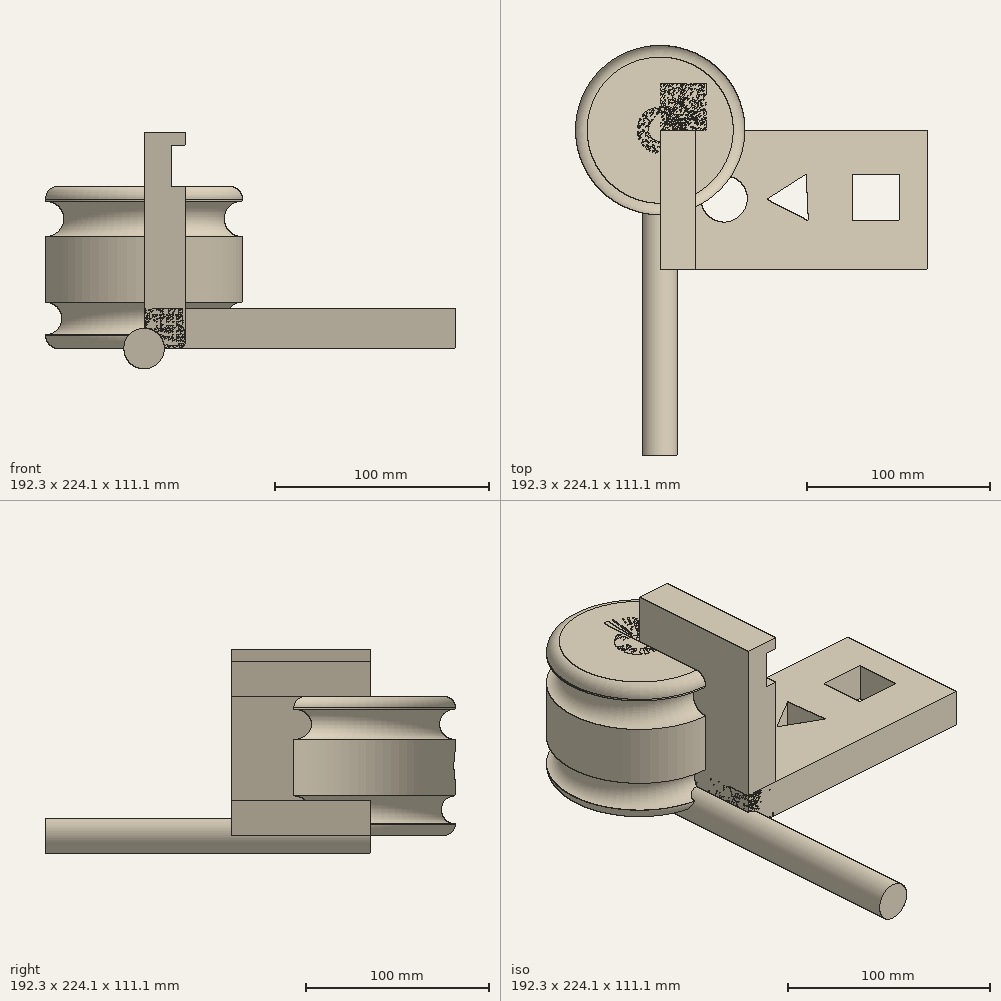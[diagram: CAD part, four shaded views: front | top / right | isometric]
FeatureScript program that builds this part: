
annotation { "Feature Type Name" : "Feature", "Feature Type Description" : "" }
export const myFeature = defineFeature(function(context is Context, id is Id, definition is map)
    precondition{}
    {
        {
            var Q0;
            Q0=qCreatedBy(makeId("Top.planeOp"),FACE);
            var sketch = newSketch(context, id + "F0", { "sketchPlane" : qUnion([Q0])});
            skCircle(sketch, "E0", {"center": v(0, 0) * mm, "radius": 12.7 * mm});
            skSolve(sketch);
        }
        {
            var Q0;
            Q0 = qSketchRegion(id + "F0", true);
            extrude(context, id + "F1", {"entities" : qUnion([Q0]), "depth" : 76.2 * mm, "offsetDistance" : 25.4 * mm});
        }
        {
            var Q0;
            Q0=qCreatedBy(makeId("Top.planeOp"),FACE);
            var sketch = newSketch(context, id + "F2", { "sketchPlane" : qUnion([Q0])});
            skLineSegment(sketch, "E1.bottom", {"start": v(0, 0) * mm, "end": v(25.4, 0) * mm});
            skLineSegment(sketch, "E1.top", {"start": v(0, 25.4) * mm, "end": v(25.4, 25.4) * mm});
            skLineSegment(sketch, "E1.left", {"start": v(0, 0) * mm, "end": v(0, 25.4) * mm});
            skLineSegment(sketch, "E1.right", {"start": v(25.4, 0) * mm, "end": v(25.4, 25.4) * mm});
            skSolve(sketch);
        }
        {
            var Q0;
            Q0 = qSketchRegion(id + "F2", true);
            extrude(context, id + "F3", {"entities" : qUnion([Q0]), "depth" : 76.2 * mm, "offsetDistance" : 25.4 * mm});
        }
        {
            var Q0;
            Q0=qCreatedBy(makeId("Top.planeOp"),FACE);
            var sketch = newSketch(context, id + "F4", { "sketchPlane" : qUnion([Q0])});
            skLineSegment(sketch, "E2", {"start": v(0, 0) * mm, "end": v(12.7, 22) * mm});
            skLineSegment(sketch, "E3", {"start": v(12.7, 22) * mm, "end": v(25.4, 0) * mm});
            skLineSegment(sketch, "E4", {"start": v(25.4, 0) * mm, "end": v(0, 0) * mm});
            skSolve(sketch);
        }
        {
            var Q0;
            Q0=makeQuery(id+"F4.imprint","IMPRINT",FACE,{"disambiguationData":[TD([[makeQuery(id+"F4.imprint","IMPRINT",EDGE,{"derivedFrom":sQuery(id+"F4.wireOp",EDGE,"E2")}),-1.0]])]});
            extrude(context, id + "F5", {"entities" : qUnion([Q0]), "depth" : 76.2 * mm, "offsetDistance" : 25.4 * mm});
        }
        {
            var Q0;
            Q0=qCreatedBy(makeId("Top.planeOp"),FACE);
            var sketch = newSketch(context, id + "F6", { "sketchPlane" : qUnion([Q0])});
            skLineSegment(sketch, "E5.bottom", {"start": v(0, 0) * mm, "end": v(146.05, 0) * mm});
            skLineSegment(sketch, "E5.top", {"start": v(0, -76.2) * mm, "end": v(146.05, -76.2) * mm});
            skLineSegment(sketch, "E5.left", {"start": v(0, 0) * mm, "end": v(0, -76.2) * mm});
            skLineSegment(sketch, "E5.right", {"start": v(146.05, 0) * mm, "end": v(146.05, -76.2) * mm});
            skCircle(sketch, "E6", {"center": v(34.93, -37.54) * mm, "radius": 12.7 * mm});
            skLineSegment(sketch, "E7.bottom", {"start": v(105.15, -49.45) * mm, "end": v(130.55, -49.45) * mm});
            skLineSegment(sketch, "E7.top", {"start": v(105.15, -24.05) * mm, "end": v(130.55, -24.05) * mm});
            skLineSegment(sketch, "E7.left", {"start": v(105.15, -49.45) * mm, "end": v(105.15, -24.05) * mm});
            skLineSegment(sketch, "E7.right", {"start": v(130.55, -49.45) * mm, "end": v(130.55, -24.05) * mm});
            skCircle(sketch, "E8.cCircle", {"center": v(73.03, -37.17) * mm, "radius": 7.33 * mm, "construction": true});
            skLineSegment(sketch, "E8.0", {"start": v(79.75, -24.13) * mm, "end": v(80.96, -49.5) * mm});
            skLineSegment(sketch, "E8.1", {"start": v(80.96, -49.5) * mm, "end": v(58.38, -37.86) * mm});
            skLineSegment(sketch, "E8.2", {"start": v(58.38, -37.86) * mm, "end": v(79.75, -24.13) * mm});
            skPoint(sketch, "E8.0.midPoint", {"position": v(80.35, -36.82) * mm});
            skSolve(sketch);
        }
        {
            var Q0;
            Q0 = qSketchRegion(id + "F6", true);
            extrude(context, id + "F7", {"entities" : qUnion([Q0]), "depth" : 19.05 * mm, "offsetDistance" : 25.4 * mm});
        }
        {
            var Q0;
            Q0=qCreatedBy(makeId("Front.planeOp"),FACE);
            var sketch = newSketch(context, id + "F8", { "sketchPlane" : qUnion([Q0])});
            skLineSegment(sketch, "E9.bottom", {"start": v(0, 0) * mm, "end": v(19.3, 0) * mm});
            skLineSegment(sketch, "E9.top", {"start": v(0, 101.6) * mm, "end": v(19.3, 101.6) * mm});
            skLineSegment(sketch, "E9.left", {"start": v(0, 0) * mm, "end": v(0, 101.6) * mm});
            skLineSegment(sketch, "E9.right", {"start": v(19.3, 0) * mm, "end": v(19.3, 101.6) * mm});
            skLineSegment(sketch, "E10.bottom", {"start": v(19.3, 95.25) * mm, "end": v(12.95, 95.25) * mm});
            skLineSegment(sketch, "E10.top", {"start": v(19.3, 76.2) * mm, "end": v(12.95, 76.2) * mm});
            skLineSegment(sketch, "E10.left", {"start": v(19.3, 95.25) * mm, "end": v(19.3, 76.2) * mm});
            skLineSegment(sketch, "E10.right", {"start": v(12.95, 95.25) * mm, "end": v(12.95, 76.2) * mm});
            skSolve(sketch);
        }
        {
            var Q0;
            {var subQ1=sQuery(id+"F8.wireOp",EDGE,"E9.bottom");Q0=makeQuery(id+"F8.imprint","IMPRINT",FACE,{"disambiguationData":[TD([[makeQuery(id+"F8.imprint","IMPRINT",EDGE,{"derivedFrom":subQ1}),1.0]])]});}
            var Q1;
            Q1 = qSketchRegion(id + "F10", true);
            extrude(context, id + "F9", {"entities" : qUnion([Q0, Q1]), "depth" : 76.2 * mm, "offsetDistance" : 25.4 * mm});
        }
        {
            var Q0;
            Q0=qCreatedBy(makeId("Front.planeOp"),FACE);
            var sketch = newSketch(context, id + "F10", { "sketchPlane" : qUnion([Q0])});
            skLineSegment(sketch, "E11.bottom", {"start": v(6.35, 0) * mm, "end": v(39.94, 0) * mm});
            skLineSegment(sketch, "E11.top", {"start": v(6.35, 76.2) * mm, "end": v(39.94, 76.2) * mm});
            skLineSegment(sketch, "E11.left", {"start": v(0, 6.35) * mm, "end": v(0, 69.85) * mm});
            skLineSegment(sketch, "E11.right", {"start": v(46.29, 6.35) * mm, "end": v(46.29, 69.85) * mm});
            skCircle(sketch, "E12", {"center": v(46.29, 86.97) * mm, "radius": 6.35 * mm});
            skCircle(sketch, "E13", {"center": v(45.89, 60.82) * mm, "radius": 8.2 * mm});
            skCircle(sketch, "E14", {"center": v(46.29, 14.1) * mm, "radius": 7.66 * mm});
            skPoint(sketch, "E15.visualSharp", {"position": v(46.29, 0) * mm});
            skArc(sketch, "E15.filletArc", {"start": v(39.94, 0) * mm, "mid": v(44.43, 1.86) * mm, "end": v(46.29, 6.35) * mm});
            skPoint(sketch, "E16.visualSharp", {"position": v(46.29, 76.2) * mm});
            skArc(sketch, "E16.filletArc", {"start": v(46.29, 69.85) * mm, "mid": v(44.43, 74.34) * mm, "end": v(39.94, 76.2) * mm});
            skPoint(sketch, "E17.visualSharp", {"position": v(0, 76.2) * mm});
            skArc(sketch, "E17.filletArc", {"start": v(6.35, 76.2) * mm, "mid": v(1.86, 74.34) * mm, "end": v(0, 69.85) * mm});
            skPoint(sketch, "E18.visualSharp", {"position": v(0, 0) * mm});
            skArc(sketch, "E18.filletArc", {"start": v(0, 6.35) * mm, "mid": v(1.86, 1.86) * mm, "end": v(6.35, 0) * mm});
            skSolve(sketch);
        }
        {
            var Q0;
            {var subQ1=sQuery(id+"F10.wireOp",EDGE,"E11.bottom");Q0=makeQuery(id+"F10.imprint","IMPRINT",FACE,{"disambiguationData":[TD([[makeQuery(id+"F10.imprint","IMPRINT",EDGE,{"derivedFrom":subQ1}),1.0]])]});}
            var Q1;
            Q1=sQuery(id+"F10.wireOp",EDGE,"E11.left");
            revolve(context, id + "F11", {"surfaceOperationType" : NewSurfaceOperationType.NEW, "entities" : qUnion([Q0]), "axis" : qUnion([Q1]), "revolveType" : RevolveType.FULL});
        }
        {
            var Q0;
            Q0=qCreatedBy(makeId("Front.planeOp"),FACE);
            var sketch = newSketch(context, id + "F12", { "sketchPlane" : qUnion([Q0])});
            skPoint(sketch, "E19", {"position": v(0, 38.1) * mm});
            skSolve(sketch);
        }
        {
            var Q0;
            Q0=sQuery(id+"F12.wireOp",VERTEX,"E19");
            var Q1;
            Q1=makeQuery(id+"F11.opRevolve","SWEPT_BODY",BODY,{"disambiguationData":[OSD([sQuery(id+"F10.wireOp",EDGE,"E11.bottom"),sQuery(id+"F10.wireOp",EDGE,"E11.top"),sQuery(id+"F10.wireOp",EDGE,"E11.left"),sQuery(id+"F10.wireOp",EDGE,"E11.right"),sQuery(id+"F10.wireOp",EDGE,"E13"),sQuery(id+"F10.wireOp",EDGE,"E14"),sQuery(id+"F10.wireOp",EDGE,"E15.filletArc"),sQuery(id+"F10.wireOp",EDGE,"E16.filletArc"),sQuery(id+"F10.wireOp",EDGE,"E17.filletArc"),sQuery(id+"F10.wireOp",EDGE,"E18.filletArc")])]});
            hole(context, id + "F13", {"style" : HoleStyle.SIMPLE, "endStyle" : HoleEndStyle.THROUGH, "standardTappedOrClearance" : lookupTablePath({ "standard" : "ANSI", "engagement" : "75%", "pitch" : "20 tpi", "size" : "3/4", "type" : "Tapped" }), "standardBlindInLast" : lookupTablePath({ "standard" : "ANSI", "engagement" : "75%", "pitch" : "20 tpi", "size" : "3/4", "type" : "Tapped" }), "holeDiameter" : 17.86 * mm, "majorDiameter" : 19.05 * mm, "showTappedDepth" : true, "isTappedThrough" : true, "tappedDepth" : 12.7 * mm, "tapClearance" : 3, "locations" : qUnion([Q0]), "scope" : qUnion([Q1])});
        }
        {
            var Q0;
            Q0=qCreatedBy(makeId("Front.planeOp"),FACE);
            var sketch = newSketch(context, id + "F14", { "sketchPlane" : qUnion([Q0])});
            skCircle(sketch, "E20", {"center": v(0, 0) * mm, "radius": 9.53 * mm});
            skSolve(sketch);
        }
        {
            var Q0;
            Q0=makeQuery(id+"F14.imprint","IMPRINT",FACE,{"disambiguationData":[TD([[makeQuery(id+"F14.imprint","IMPRINT",EDGE,{"derivedFrom":sQuery(id+"F14.wireOp",EDGE,"E20")}),1.0]])]});
            extrude(context, id + "F15", {"entities" : qUnion([Q0]), "depth" : 177.8 * mm, "offsetDistance" : 25.4 * mm});
        }
    });
